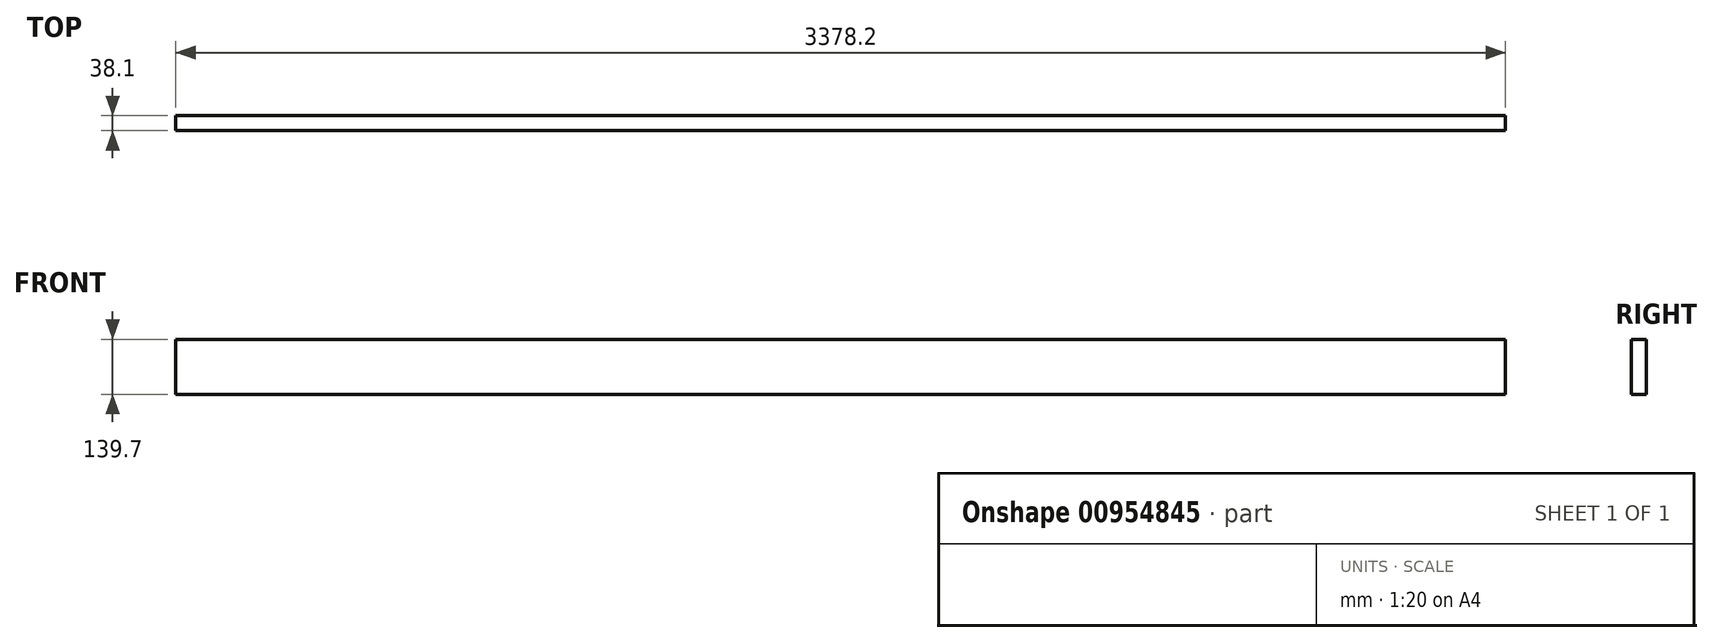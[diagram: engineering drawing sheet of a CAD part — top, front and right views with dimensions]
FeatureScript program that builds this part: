
annotation { "Feature Type Name" : "Feature", "Feature Type Description" : "" }
export const myFeature = defineFeature(function(context is Context, id is Id, definition is map)
    precondition{}
    {
        {
            var Q0;
            Q0=qCreatedBy(makeId("Right.planeOp"),FACE);
            var sketch = newSketch(context, id + "F0", { "sketchPlane" : qUnion([Q0])});
            skLineSegment(sketch, "E0.bottom", {"start": v(-19.05, 69.85) * mm, "end": v(19.05, 69.85) * mm});
            skLineSegment(sketch, "E0.top", {"start": v(-19.05, -69.85) * mm, "end": v(19.05, -69.85) * mm});
            skLineSegment(sketch, "E0.left", {"start": v(-19.05, 69.85) * mm, "end": v(-19.05, -69.85) * mm});
            skLineSegment(sketch, "E0.right", {"start": v(19.05, 69.85) * mm, "end": v(19.05, -69.85) * mm});
            skPoint(sketch, "E1", {"position": v(0, 69.85) * mm});
            skPoint(sketch, "E2", {"position": v(-19.05, 0) * mm});
            skSolve(sketch);
        }
        {
            var Q0;
            Q0=qSketchRegion(id+"F0",true);
            extrude(context, id + "F1", {"entities" : qUnion([Q0]), "endBound" : BoundingType.SYMMETRIC, "depth" : 3378.2 * mm, "offsetDistance" : 25.4 * mm, "hasSecondDirection" : true, "secondDirectionOppositeDirection" : true, "secondDirectionDepth" : 609.6 * mm});
        }
    });
